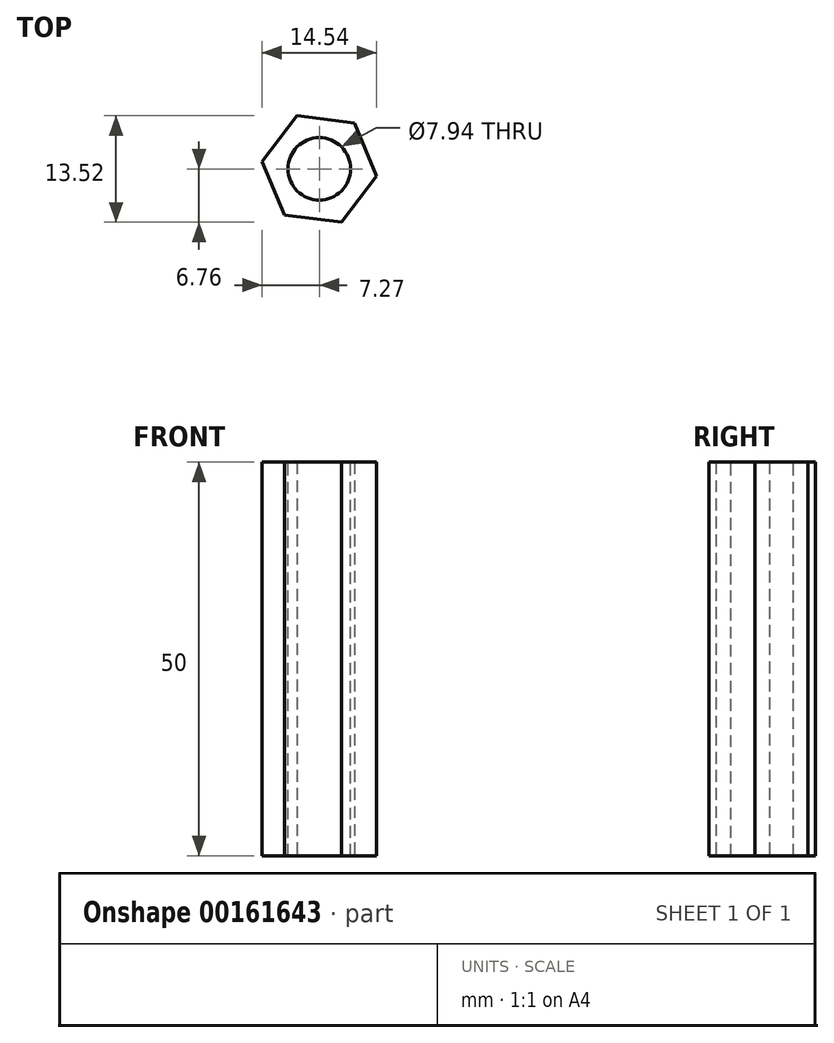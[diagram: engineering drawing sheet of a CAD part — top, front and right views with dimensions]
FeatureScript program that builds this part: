
annotation { "Feature Type Name" : "Feature", "Feature Type Description" : "" }
export const myFeature = defineFeature(function(context is Context, id is Id, definition is map)
    precondition{}
    {
        {
            var Q0;
            Q0=qCreatedBy(makeId("Top.planeOp"),FACE);
            var sketch = newSketch(context, id + "F0", { "sketchPlane" : qUnion([Q0])});
            skCircle(sketch, "E0.cCircle", {"center": v(0, 0) * mm, "radius": 6.35 * mm, "construction": true});
            skLineSegment(sketch, "E0.0", {"start": v(-7.27, 0.93) * mm, "end": v(-2.83, 6.76) * mm});
            skLineSegment(sketch, "E0.1", {"start": v(-2.83, 6.76) * mm, "end": v(4.44, 5.83) * mm});
            skLineSegment(sketch, "E0.2", {"start": v(4.44, 5.83) * mm, "end": v(7.27, -0.93) * mm});
            skLineSegment(sketch, "E0.3", {"start": v(7.27, -0.93) * mm, "end": v(2.83, -6.76) * mm});
            skLineSegment(sketch, "E0.4", {"start": v(2.83, -6.76) * mm, "end": v(-4.44, -5.83) * mm});
            skLineSegment(sketch, "E0.5", {"start": v(-4.44, -5.83) * mm, "end": v(-7.27, 0.93) * mm});
            skPoint(sketch, "E0.0.midPoint", {"position": v(-5.05, 3.85) * mm});
            skSolve(sketch);
        }
        {
            var Q0;
            Q0 = qSketchRegion(id + "F0", true);
            extrude(context, id + "F1", {"entities" : qUnion([Q0]), "endBound" : BoundingType.SYMMETRIC, "depth" : 50 * mm});
        }
        {
            var Q0;
            Q0=makeQuery(id+"F1.opExtrude","CAP_FACE",FACE,{"disambiguationData":[OSD([sQuery(id+"F0.wireOp",EDGE,"E0.0"),sQuery(id+"F0.wireOp",EDGE,"E0.1"),sQuery(id+"F0.wireOp",EDGE,"E0.2"),sQuery(id+"F0.wireOp",EDGE,"E0.3"),sQuery(id+"F0.wireOp",EDGE,"E0.4"),sQuery(id+"F0.wireOp",EDGE,"E0.5")])],"isStart":false});
            var sketch = newSketch(context, id + "F2", { "sketchPlane" : qUnion([Q0])});
            skCircle(sketch, "E1", {"center": v(0, 0) * mm, "radius": 3.97 * mm});
            skSolve(sketch);
        }
        {
            var Q0;
            Q0 = qSketchRegion(id + "F2", true);
            extrude(context, id + "F3", {"entities" : qUnion([Q0]), "operationType" : NewBodyOperationType.REMOVE, "endBound" : BoundingType.THROUGH_ALL, "oppositeDirection" : true, "depth" : 25 * mm});
        }
    });
